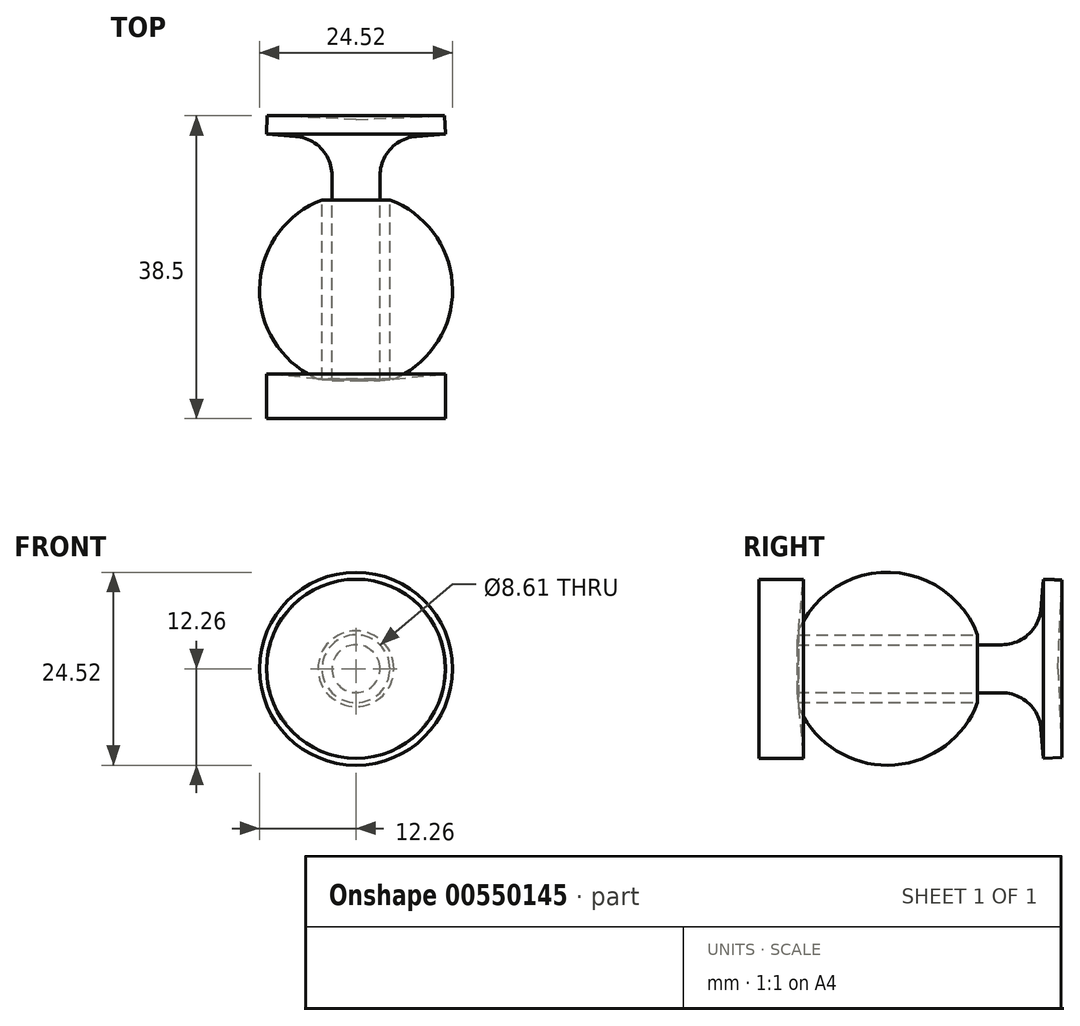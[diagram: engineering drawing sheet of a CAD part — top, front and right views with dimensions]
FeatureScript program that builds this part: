
annotation { "Feature Type Name" : "Feature", "Feature Type Description" : "" }
export const myFeature = defineFeature(function(context is Context, id is Id, definition is map)
    precondition{}
    {
        {
            var Q0;
            Q0=qCreatedBy(makeId("Top.planeOp"),FACE);
            var sketch = newSketch(context, id + "F0", { "sketchPlane" : qUnion([Q0])});
            skArc(sketch, "E0", {"start": v(-4.3, 11.47) * mm, "mid": v(-12.26, 0) * mm, "end": v(-4.3, -11.47) * mm});
            skLineSegment(sketch, "E1.left", {"start": v(4.3, -11.47) * mm, "end": v(4.3, 11.47) * mm});
            skLineSegment(sketch, "E1.right", {"start": v(-4.3, -11.47) * mm, "end": v(-4.3, 16.25) * mm});
            skArc(sketch, "E2.trimOffspring", {"start": v(4.3, -11.47) * mm, "mid": v(12.26, 0) * mm, "end": v(4.3, 11.47) * mm});
            skLineSegment(sketch, "E3", {"start": v(11.37, 19.84) * mm, "end": v(7.66, 19.54) * mm});
            skPoint(sketch, "E4.orphan", {"position": v(4.3, 16.25) * mm});
            skPoint(sketch, "E5.orphan", {"position": v(4.3, -16.25) * mm});
            skPoint(sketch, "E6.orphan", {"position": v(-4.3, -16.25) * mm});
            skLineSegment(sketch, "E7", {"start": v(11.37, 19.84) * mm, "end": v(11.27, 22.18) * mm});
            skLineSegment(sketch, "E8", {"start": v(11.27, 22.18) * mm, "end": v(0, 21.67) * mm});
            skLineSegment(sketch, "E9", {"start": v(0, 21.67) * mm, "end": v(0, -16.32) * mm});
            skLineSegment(sketch, "E10", {"start": v(0, -16.32) * mm, "end": v(11.37, -16.32) * mm});
            skLineSegment(sketch, "E11", {"start": v(11.37, -16.32) * mm, "end": v(11.37, -10.63) * mm});
            skLineSegment(sketch, "E12", {"start": v(11.37, -10.63) * mm, "end": v(3.04, -11.44) * mm});
            skLineSegment(sketch, "E13", {"start": v(3.05, 14.56) * mm, "end": v(3.04, -11.44) * mm});
            skPoint(sketch, "E14.visualSharp", {"position": v(3.05, 19.18) * mm});
            skArc(sketch, "E14.filletArc", {"start": v(7.66, 19.54) * mm, "mid": v(4.38, 17.95) * mm, "end": v(3.05, 14.56) * mm});
            skSolve(sketch);
        }
        {
            var Q0;
            Q0=makeQuery(id+"F0.imprint","IMPRINT",FACE,{"disambiguationData":[TD([[makeQuery(id+"F0.imprint","IMPRINT",EDGE,{"derivedFrom":sQuery(id+"F0.wireOp",EDGE,"E1.left")}),-1.0]])]});
            var Q1;
            Q1=makeQuery(id+"F0.imprint","IMPRINT",FACE,{"disambiguationData":[TD([[makeQuery(id+"F0.imprint","IMPRINT",EDGE,{"derivedFrom":sQuery(id+"F0.wireOp",EDGE,"E3")}),-1.0]])]});
            var Q2;
            Q2=sQuery(id+"F0.wireOp",EDGE,"E9");
            revolve(context, id + "F1", {"entities" : qUnion([Q0, Q1]), "axis" : qUnion([Q2]), "revolveType" : RevolveType.FULL});
        }
    });
